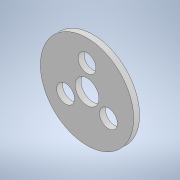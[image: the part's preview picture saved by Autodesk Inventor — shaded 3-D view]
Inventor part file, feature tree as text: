
AUTODESK INVENTOR PART (.ipt)
format: ipt  version: 2022 (Build 260153000, 153)  size: 119,296 bytes
history: native  units: in
note: dims shown in document units (in); Inventor stores cm internally (conversion verified against a paired STEP export)
features: extrude x2
ambient origin geometry x8: Origin, YZ Plane, XZ Plane, XY Plane, X Axis, Y Axis, Z Axis, Center Point
bodies: Solid1 (feature_tree)
feature tree (2):
  extrude  "Extrusion1"  Depth=0.9843in
  extrude  "Extrusion2"  Depth=0.1181in TaperAngle=0.0deg
